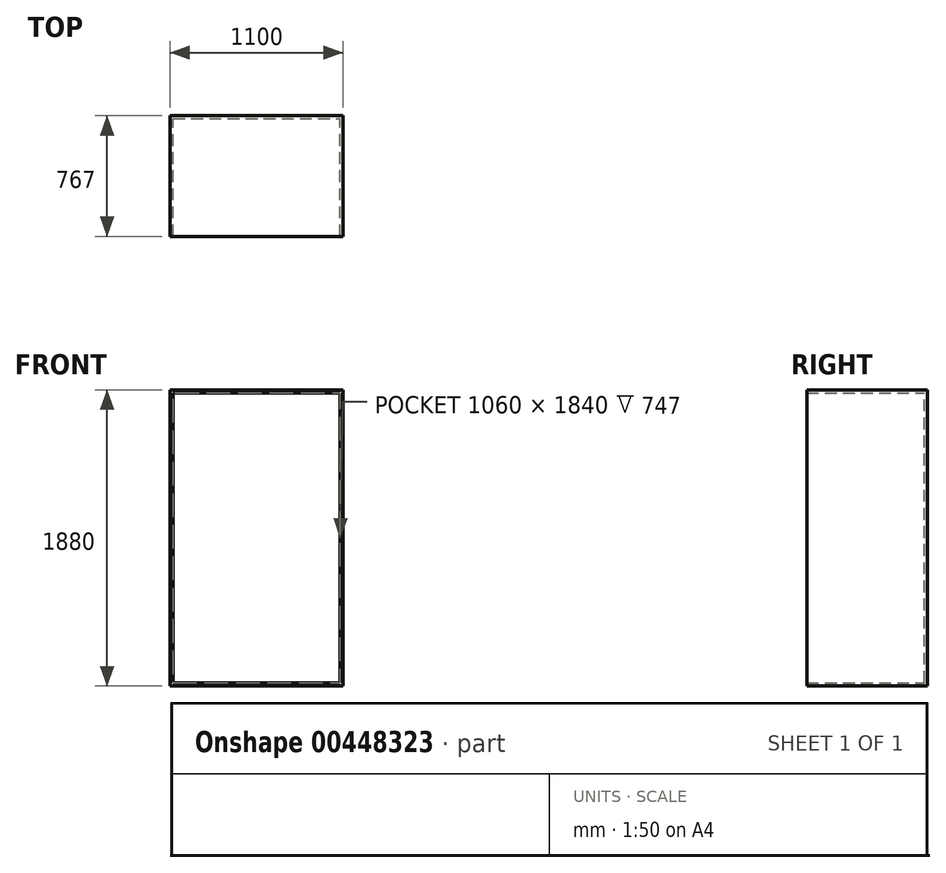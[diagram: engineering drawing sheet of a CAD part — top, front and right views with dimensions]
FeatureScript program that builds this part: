
annotation { "Feature Type Name" : "Feature", "Feature Type Description" : "" }
export const myFeature = defineFeature(function(context is Context, id is Id, definition is map)
    precondition{}
    {
        {
            var Q0;
            Q0=qCreatedBy(makeId("Front.planeOp"),FACE);
            var sketch = newSketch(context, id + "F0", { "sketchPlane" : qUnion([Q0])});
            skLineSegment(sketch, "E0.bottom", {"start": v(0, 0) * mm, "end": v(1060, 0) * mm});
            skLineSegment(sketch, "E0.top", {"start": v(0, 1840) * mm, "end": v(1060, 1840) * mm});
            skLineSegment(sketch, "E0.left", {"start": v(0, 0) * mm, "end": v(0, 1840) * mm});
            skLineSegment(sketch, "E0.right", {"start": v(1060, 0) * mm, "end": v(1060, 1840) * mm});
            skSolve(sketch);
        }
        {
            var Q0;
            Q0=makeQuery(id+"F0.imprint","IMPRINT",FACE,{"disambiguationData":[TD([[makeQuery(id+"F0.imprint","IMPRINT",EDGE,{"derivedFrom":sQuery(id+"F0.wireOp",EDGE,"E0.bottom")}),1.0]])]});
            var sketch = newSketch(context, id + "F1", { "sketchPlane" : qUnion([Q0])});
            skLineSegment(sketch, "E1.0", {"start": v(1080, 1860) * mm, "end": v(-20, 1860) * mm});
            skLineSegment(sketch, "E1.1", {"start": v(1080, -20) * mm, "end": v(1080, 1860) * mm});
            skLineSegment(sketch, "E1.2", {"start": v(-20, -20) * mm, "end": v(1080, -20) * mm});
            skLineSegment(sketch, "E1.3", {"start": v(-20, 1860) * mm, "end": v(-20, -20) * mm});
            skSolve(sketch);
        }
        {
            var Q0;
            Q0=makeQuery(id+"F1.imprint","IMPRINT",FACE,{"disambiguationData":[TD([[makeQuery(id+"F1.imprint","IMPRINT",EDGE,{"derivedFrom":sQuery(id+"F1.wireOp",EDGE,"E1.0")}),1.0]])]});
            extrude(context, id + "F2", {"entities" : qUnion([Q0]), "depth" : 747 * mm});
        }
        {
            var Q0;
            Q0=makeQuery(id+"F2.opExtrude","CAP_FACE",FACE,{"disambiguationData":[OSD([sQuery(id+"F0.wireOp",EDGE,"E0.bottom"),sQuery(id+"F0.wireOp",EDGE,"E0.top"),sQuery(id+"F0.wireOp",EDGE,"E0.left"),sQuery(id+"F0.wireOp",EDGE,"E0.right"),sQuery(id+"F1.wireOp",EDGE,"E1.0"),sQuery(id+"F1.wireOp",EDGE,"E1.1"),sQuery(id+"F1.wireOp",EDGE,"E1.2"),sQuery(id+"F1.wireOp",EDGE,"E1.3")])],"isStart":true});
            var sketch = newSketch(context, id + "F3", { "sketchPlane" : qUnion([Q0])});
            skLineSegment(sketch, "E2.bottom", {"start": v(-1080, 1860) * mm, "end": v(20, 1860) * mm});
            skLineSegment(sketch, "E2.top", {"start": v(-1080, -20) * mm, "end": v(20, -20) * mm});
            skLineSegment(sketch, "E2.left", {"start": v(-1080, 1860) * mm, "end": v(-1080, -20) * mm});
            skLineSegment(sketch, "E2.right", {"start": v(20, 1860) * mm, "end": v(20, -20) * mm});
            skSolve(sketch);
        }
        {
            var Q0;
            Q0 = qSketchRegion(id + "F3", true);
            extrude(context, id + "F4", {"entities" : qUnion([Q0]), "operationType" : NewBodyOperationType.ADD, "depth" : 20 * mm});
        }
    });
